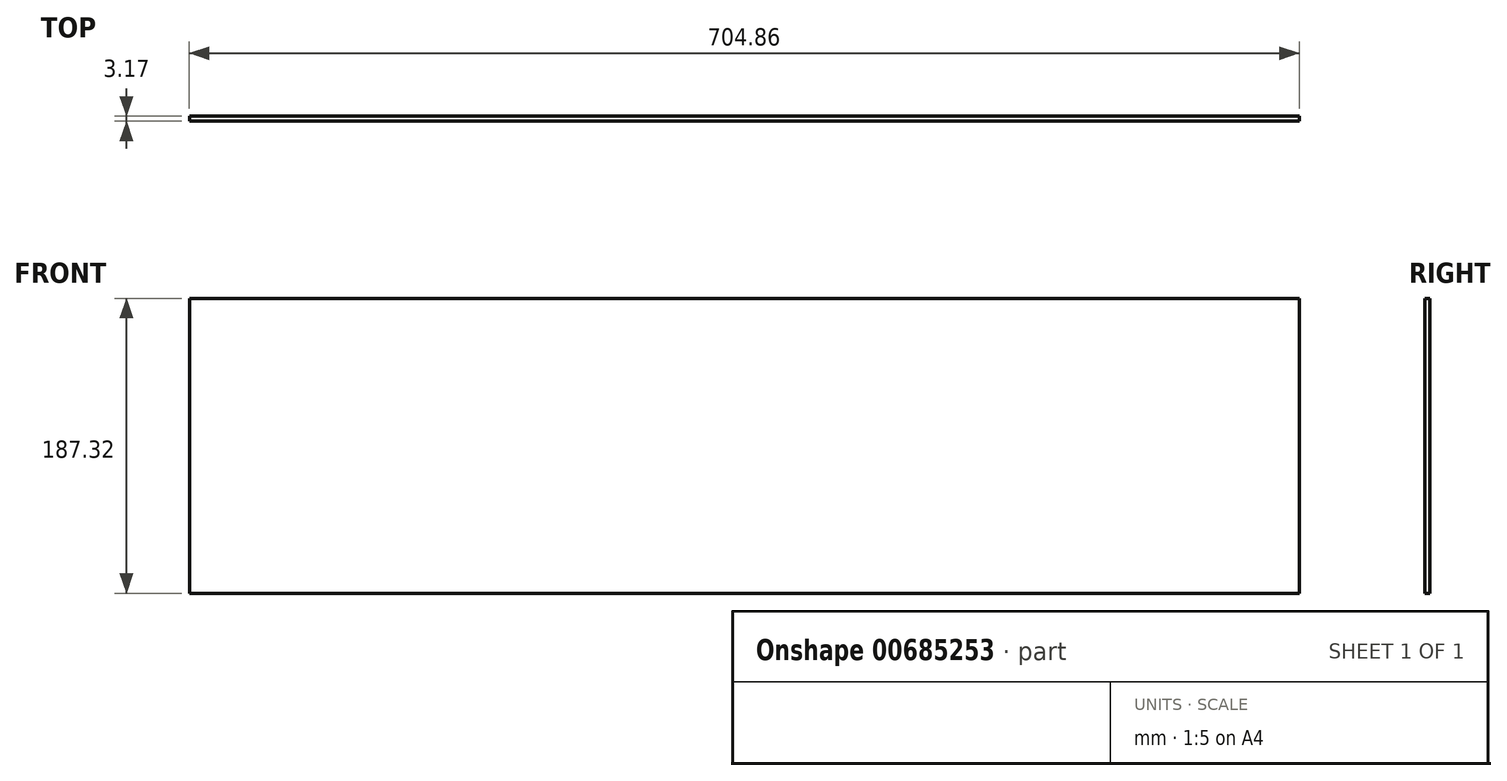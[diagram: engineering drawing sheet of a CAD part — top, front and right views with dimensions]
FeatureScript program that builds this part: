
annotation { "Feature Type Name" : "Feature", "Feature Type Description" : "" }
export const myFeature = defineFeature(function(context is Context, id is Id, definition is map)
    precondition{}
    {
        {
            var Q0;
            Q0=qCreatedBy(makeId("Front.planeOp"),FACE);
            var sketch = newSketch(context, id + "F0", { "sketchPlane" : qUnion([Q0])});
            skLineSegment(sketch, "E0.bottom", {"start": v(352.43, 93.66) * mm, "end": v(-352.43, 93.66) * mm});
            skLineSegment(sketch, "E0.top", {"start": v(352.43, -93.66) * mm, "end": v(-352.43, -93.66) * mm});
            skLineSegment(sketch, "E0.left", {"start": v(352.43, 93.66) * mm, "end": v(352.43, -93.66) * mm});
            skLineSegment(sketch, "E0.right", {"start": v(-352.43, 93.66) * mm, "end": v(-352.43, -93.66) * mm});
            skPoint(sketch, "E0.middle", {"position": v(0, 0) * mm});
            skSolve(sketch);
        }
        {
            var Q0;
            Q0=qSketchRegion(id+"F0",true);
            extrude(context, id + "F1", {"entities" : qUnion([Q0]), "depth" : 3.17 * mm, "offsetDistance" : 25.4 * mm});
        }
    });
